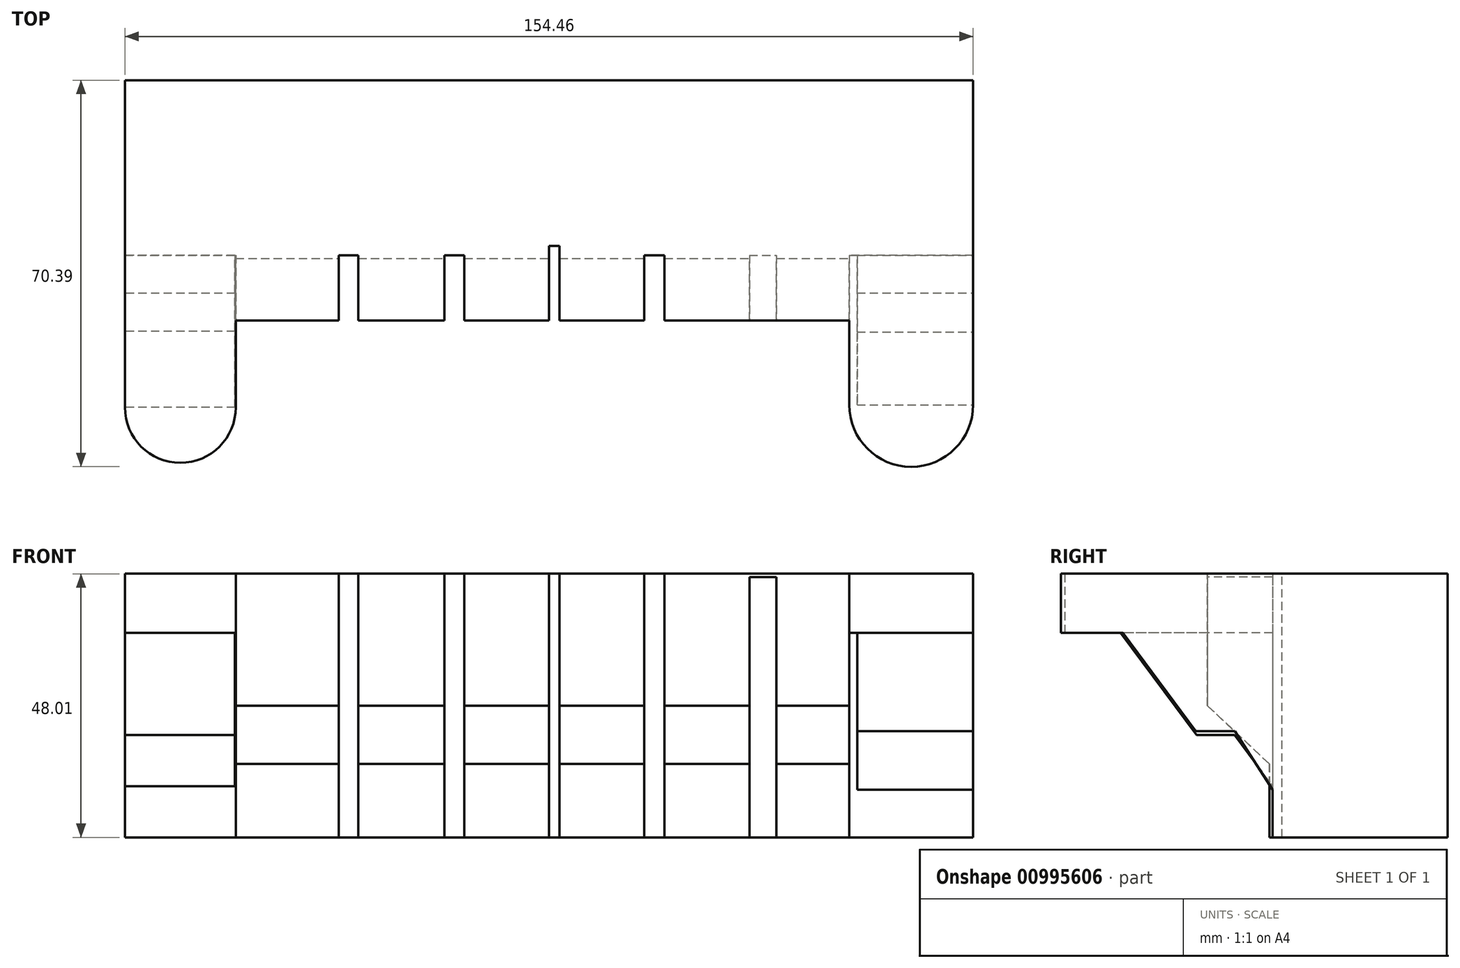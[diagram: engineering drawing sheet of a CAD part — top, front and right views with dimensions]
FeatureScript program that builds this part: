
annotation { "Feature Type Name" : "Feature", "Feature Type Description" : "" }
export const myFeature = defineFeature(function(context is Context, id is Id, definition is map)
    precondition{}
    {
        {
            var Q0;
            Q0=qCreatedBy(makeId("Top.planeOp"),FACE);
            var sketch = newSketch(context, id + "F0", { "sketchPlane" : qUnion([Q0])});
            skLineSegment(sketch, "E0.bottom", {"start": v(-77.23, 15.64) * mm, "end": v(77.23, 15.64) * mm});
            skLineSegment(sketch, "E0.top", {"start": v(-77.23, -16.82) * mm, "end": v(77.23, -16.82) * mm});
            skLineSegment(sketch, "E0.left", {"start": v(-77.23, 15.64) * mm, "end": v(-77.23, -16.82) * mm});
            skLineSegment(sketch, "E0.right", {"start": v(77.23, 15.64) * mm, "end": v(77.23, -16.82) * mm});
            skSolve(sketch);
        }
        {
            var Q0;
            Q0=makeQuery(id+"F0.imprint","IMPRINT",FACE,{"disambiguationData":[TD([[makeQuery(id+"F0.imprint","IMPRINT",EDGE,{"derivedFrom":sQuery(id+"F0.wireOp",EDGE,"E0.bottom")}),-1.0]])]});
            extrude(context, id + "F1", {"entities" : qUnion([Q0]), "depth" : 48 * mm, "offsetDistance" : 25.4 * mm});
        }
        {
            var Q0;
            Q0=makeQuery(id+"F1.opExtrude","SWEPT_FACE",FACE,{"disambiguationData":[OSD([sQuery(id+"F0.wireOp",EDGE,"E0.right")])]});
            var sketch = newSketch(context, id + "F2", { "sketchPlane" : qUnion([Q0])});
            skPoint(sketch, "E1.oppositeSnap0", {"position": v(15.64, 24) * mm});
            skLineSegment(sketch, "E1.bottom", {"start": v(-16.82, 48.01) * mm, "end": v(-28.1, 48.01) * mm});
            skLineSegment(sketch, "E1.top", {"start": v(-16.82, 24) * mm, "end": v(-28.1, 24) * mm});
            skLineSegment(sketch, "E1.left", {"start": v(-16.82, 48.01) * mm, "end": v(-16.82, 24) * mm});
            skLineSegment(sketch, "E1.right", {"start": v(-28.1, 48.01) * mm, "end": v(-28.1, 24) * mm});
            skLineSegment(sketch, "E2", {"start": v(-28.1, 24) * mm, "end": v(-16.45, 13.01) * mm});
            skLineSegment(sketch, "E3", {"start": v(-16.45, 13.01) * mm, "end": v(-16.82, 24) * mm});
            skSolve(sketch);
        }
        {
            var Q0;
            Q0=makeQuery(id+"F2.imprint","IMPRINT",FACE,{"disambiguationData":[TD([[makeQuery(id+"F2.imprint","IMPRINT",EDGE,{"derivedFrom":sQuery(id+"F2.wireOp",EDGE,"E1.bottom")}),1.0]])]});
            var Q1;
            {var subQ0=sQuery(id+"F2.wireOp",EDGE,"E1.top");Q1=makeQuery(id+"F2.imprint","IMPRINT",FACE,{"disambiguationData":[TD([[makeQuery(id+"F2.imprint","IMPRINT",EDGE,{"derivedFrom":subQ0}),1.0]])]});}
            extrude(context, id + "F3", {"entities" : qUnion([Q0, Q1]), "operationType" : NewBodyOperationType.ADD, "oppositeDirection" : true, "depth" : 154.68 * mm, "offsetDistance" : 25.4 * mm});
        }
        {
            var Q0;
            Q0=makeQuery(id+"F3.opExtrude","SWEPT_FACE",FACE,{"disambiguationData":[OSD([sQuery(id+"F2.wireOp",EDGE,"E1.right")])]});
            var sketch = newSketch(context, id + "F4", { "sketchPlane" : qUnion([Q0])});
            skLineSegment(sketch, "E4.bottom", {"start": v(-77.45, 48.01) * mm, "end": v(-57.04, 48.01) * mm});
            skLineSegment(sketch, "E4.top", {"start": v(-77.45, 0) * mm, "end": v(-57.04, 0) * mm});
            skLineSegment(sketch, "E4.left", {"start": v(-77.45, 48.01) * mm, "end": v(-77.45, 0) * mm});
            skLineSegment(sketch, "E4.right", {"start": v(-57.04, 48.01) * mm, "end": v(-57.04, 0) * mm});
            skLineSegment(sketch, "E5.bottom", {"start": v(77.23, 48.01) * mm, "end": v(54.67, 48.01) * mm});
            skLineSegment(sketch, "E5.top", {"start": v(77.23, 0) * mm, "end": v(54.67, 0) * mm});
            skLineSegment(sketch, "E5.left", {"start": v(77.23, 48.01) * mm, "end": v(77.23, 0) * mm});
            skLineSegment(sketch, "E5.right", {"start": v(54.67, 48.01) * mm, "end": v(54.67, 0) * mm});
            skLineSegment(sketch, "E6.bottom", {"start": v(-38.3, 48.01) * mm, "end": v(-34.74, 48.01) * mm});
            skLineSegment(sketch, "E6.top", {"start": v(-38.3, 0) * mm, "end": v(-34.74, 0) * mm});
            skLineSegment(sketch, "E6.left", {"start": v(-38.3, 48.01) * mm, "end": v(-38.3, 0) * mm});
            skLineSegment(sketch, "E6.right", {"start": v(-34.74, 48.01) * mm, "end": v(-34.74, 0) * mm});
            skLineSegment(sketch, "E7.bottom", {"start": v(-19.02, 48.01) * mm, "end": v(-15.44, 48.01) * mm});
            skLineSegment(sketch, "E7.top", {"start": v(-19.02, 0) * mm, "end": v(-15.44, 0) * mm});
            skLineSegment(sketch, "E7.left", {"start": v(-19.02, 48.01) * mm, "end": v(-19.02, 0) * mm});
            skLineSegment(sketch, "E7.right", {"start": v(-15.44, 48.01) * mm, "end": v(-15.44, 0) * mm});
            skLineSegment(sketch, "E8.bottom", {"start": v(-0.1, 48.01) * mm, "end": v(0, 48.01) * mm});
            skLineSegment(sketch, "E8.top", {"start": v(-0.1, 0) * mm, "end": v(0, 0) * mm});
            skLineSegment(sketch, "E8.left", {"start": v(-0.1, 48.01) * mm, "end": v(-0.1, 0) * mm});
            skLineSegment(sketch, "E8.right", {"start": v(0, 48.01) * mm, "end": v(0, 0) * mm});
            skLineSegment(sketch, "E9.bottom", {"start": v(17.33, 48.01) * mm, "end": v(21.02, 48.01) * mm});
            skLineSegment(sketch, "E9.top", {"start": v(17.33, 0) * mm, "end": v(21.02, 0) * mm});
            skLineSegment(sketch, "E9.left", {"start": v(17.33, 48.01) * mm, "end": v(17.33, 0) * mm});
            skLineSegment(sketch, "E9.right", {"start": v(21.02, 48.01) * mm, "end": v(21.02, 0) * mm});
            skLineSegment(sketch, "E10.bottom", {"start": v(36.5, 47.4) * mm, "end": v(41.4, 47.4) * mm});
            skLineSegment(sketch, "E10.top", {"start": v(36.5, 0) * mm, "end": v(41.4, 0) * mm});
            skLineSegment(sketch, "E10.left", {"start": v(36.5, 47.4) * mm, "end": v(36.5, 0) * mm});
            skLineSegment(sketch, "E10.right", {"start": v(41.4, 47.4) * mm, "end": v(41.4, 0) * mm});
            skSolve(sketch);
        }
        {
            var Q0;
            {var subQ0=sQuery(id+"F4.wireOp",EDGE,"E4.top");Q0=makeQuery(id+"F4.imprint","IMPRINT",FACE,{"disambiguationData":[TD([[makeQuery(id+"F4.imprint","IMPRINT",EDGE,{"derivedFrom":subQ0}),1.0]])]});}
            var Q1;
            {var subQ0=sQuery(id+"F4.wireOp",EDGE,"E4.bottom");Q1=makeQuery(id+"F4.imprint","IMPRINT",FACE,{"disambiguationData":[TD([[makeQuery(id+"F4.imprint","IMPRINT",EDGE,{"derivedFrom":subQ0}),-1.0]])]});}
            var Q2;
            {var subQ0=sQuery(id+"F4.wireOp",EDGE,"E6.top");Q2=makeQuery(id+"F4.imprint","IMPRINT",FACE,{"disambiguationData":[TD([[makeQuery(id+"F4.imprint","IMPRINT",EDGE,{"derivedFrom":subQ0}),1.0]])]});}
            var Q3;
            {var subQ0=sQuery(id+"F4.wireOp",EDGE,"E6.bottom");Q3=makeQuery(id+"F4.imprint","IMPRINT",FACE,{"disambiguationData":[TD([[makeQuery(id+"F4.imprint","IMPRINT",EDGE,{"derivedFrom":subQ0}),-1.0]])]});}
            var Q4;
            {var subQ0=sQuery(id+"F4.wireOp",EDGE,"E7.bottom");Q4=makeQuery(id+"F4.imprint","IMPRINT",FACE,{"disambiguationData":[TD([[makeQuery(id+"F4.imprint","IMPRINT",EDGE,{"derivedFrom":subQ0}),-1.0]])]});}
            var Q5;
            {var subQ0=sQuery(id+"F4.wireOp",EDGE,"E7.top");Q5=makeQuery(id+"F4.imprint","IMPRINT",FACE,{"disambiguationData":[TD([[makeQuery(id+"F4.imprint","IMPRINT",EDGE,{"derivedFrom":subQ0}),1.0]])]});}
            var Q6;
            {var subQ0=sQuery(id+"F4.wireOp",EDGE,"E9.bottom");Q6=makeQuery(id+"F4.imprint","IMPRINT",FACE,{"disambiguationData":[TD([[makeQuery(id+"F4.imprint","IMPRINT",EDGE,{"derivedFrom":subQ0}),-1.0]])]});}
            var Q7;
            {var subQ0=sQuery(id+"F4.wireOp",EDGE,"E9.top");Q7=makeQuery(id+"F4.imprint","IMPRINT",FACE,{"disambiguationData":[TD([[makeQuery(id+"F4.imprint","IMPRINT",EDGE,{"derivedFrom":subQ0}),1.0]])]});}
            var Q8;
            {var subQ0=sQuery(id+"F4.wireOp",EDGE,"E10.top");Q8=makeQuery(id+"F4.imprint","IMPRINT",FACE,{"disambiguationData":[TD([[makeQuery(id+"F4.imprint","IMPRINT",EDGE,{"derivedFrom":subQ0}),1.0]])]});}
            var Q9;
            {var subQ0=sQuery(id+"F4.wireOp",EDGE,"E5.bottom");Q9=makeQuery(id+"F4.imprint","IMPRINT",FACE,{"disambiguationData":[TD([[makeQuery(id+"F4.imprint","IMPRINT",EDGE,{"derivedFrom":subQ0}),-1.0]])]});}
            var Q10;
            {var subQ0=sQuery(id+"F4.wireOp",EDGE,"E5.top");Q10=makeQuery(id+"F4.imprint","IMPRINT",FACE,{"disambiguationData":[TD([[makeQuery(id+"F4.imprint","IMPRINT",EDGE,{"derivedFrom":subQ0}),-1.0]])]});}
            var Q11;
            {var subQ0=sQuery(id+"F4.wireOp",EDGE,"E10.bottom");Q11=makeQuery(id+"F4.imprint","IMPRINT",FACE,{"disambiguationData":[TD([[makeQuery(id+"F4.imprint","IMPRINT",EDGE,{"derivedFrom":subQ0}),-1.0]])]});}
            extrude(context, id + "F5", {"entities" : qUnion([Q0, Q1, Q2, Q3, Q4, Q5, Q6, Q7, Q8, Q9, Q10, Q11]), "operationType" : NewBodyOperationType.REMOVE, "oppositeDirection" : true, "depth" : 11.88 * mm, "offsetDistance" : 25.4 * mm});
        }
        {
            var Q0;
            Q0=makeQuery(id+"F3.boolean.opBoolean","MERGE",FACE,{"derivedFrom":[makeQuery(id+"F1.opExtrude","CAP_FACE",FACE,{"disambiguationData":[OSD([sQuery(id+"F0.wireOp",EDGE,"E0.bottom"),sQuery(id+"F0.wireOp",EDGE,"E0.top"),sQuery(id+"F0.wireOp",EDGE,"E0.left"),sQuery(id+"F0.wireOp",EDGE,"E0.right")])],"isStart":false}),makeQuery(id+"F3.opExtrude","SWEPT_FACE",FACE,{"disambiguationData":[OSD([sQuery(id+"F2.wireOp",EDGE,"E1.bottom")])]})]});
            var sketch = newSketch(context, id + "F6", { "sketchPlane" : qUnion([Q0])});
            skLineSegment(sketch, "E11.bottom", {"start": v(-77.23, -16.21) * mm, "end": v(-57.04, -16.21) * mm});
            skLineSegment(sketch, "E11.top", {"start": v(-77.23, -43.94) * mm, "end": v(-57.04, -43.94) * mm});
            skLineSegment(sketch, "E11.left", {"start": v(-77.23, -16.21) * mm, "end": v(-77.23, -43.94) * mm});
            skLineSegment(sketch, "E11.right", {"start": v(-57.04, -16.21) * mm, "end": v(-57.04, -43.94) * mm});
            skArc(sketch, "E12", {"start": v(-77.23, -43.94) * mm, "mid": v(-67.14, -54.03) * mm, "end": v(-57.04, -43.94) * mm});
            skPoint(sketch, "E13.oppositeSnap0", {"position": v(77.23, -0.29) * mm});
            skLineSegment(sketch, "E13.bottom", {"start": v(54.67, -16.21) * mm, "end": v(77.23, -16.21) * mm});
            skLineSegment(sketch, "E13.top", {"start": v(54.67, -43.47) * mm, "end": v(77.23, -43.47) * mm});
            skLineSegment(sketch, "E13.left", {"start": v(54.67, -16.21) * mm, "end": v(54.67, -43.47) * mm});
            skLineSegment(sketch, "E13.right", {"start": v(77.23, -16.21) * mm, "end": v(77.23, -43.47) * mm});
            skArc(sketch, "E14", {"start": v(54.67, -43.47) * mm, "mid": v(65.95, -54.75) * mm, "end": v(77.23, -43.47) * mm});
            skSolve(sketch);
        }
        {
            var Q0;
            {var subQ5=sQuery(id+"F6.wireOp",EDGE,"E11.bottom");Q0=makeQuery(id+"F6.imprint","IMPRINT",FACE,{"disambiguationData":[TD([[makeQuery(id+"F6.imprint","IMPRINT",EDGE,{"derivedFrom":subQ5}),-1.0]])]});}
            var Q1;
            Q1=makeQuery(id+"F6.imprint","IMPRINT",FACE,{"disambiguationData":[TD([[makeQuery(id+"F6.imprint","IMPRINT",EDGE,{"derivedFrom":sQuery(id+"F6.wireOp",EDGE,"E11.top")}),-1.0]])]});
            var Q2;
            Q2=makeQuery(id+"F6.imprint","IMPRINT",FACE,{"disambiguationData":[TD([[makeQuery(id+"F6.imprint","IMPRINT",EDGE,{"derivedFrom":sQuery(id+"F6.wireOp",EDGE,"E13.top")}),-1.0]])]});
            var Q3;
            {var subQ4=sQuery(id+"F6.wireOp",EDGE,"E13.bottom");Q3=makeQuery(id+"F6.imprint","IMPRINT",FACE,{"disambiguationData":[TD([[makeQuery(id+"F6.imprint","IMPRINT",EDGE,{"derivedFrom":subQ4}),-1.0]])]});}
            extrude(context, id + "F7", {"entities" : qUnion([Q0, Q1, Q2, Q3]), "operationType" : NewBodyOperationType.ADD, "oppositeDirection" : true, "depth" : 10.77 * mm, "offsetDistance" : 25.4 * mm});
        }
        {
            var Q0;
            Q0=makeQuery(id+"F7.boolean.opBoolean","MERGE",FACE,{"derivedFrom":[makeQuery(id+"F1.opExtrude","SWEPT_FACE",FACE,{"disambiguationData":[OSD([sQuery(id+"F0.wireOp",EDGE,"E0.left")])]}),makeQuery(id+"F7.opExtrude","SWEPT_FACE",FACE,{"disambiguationData":[OSD([sQuery(id+"F6.wireOp",EDGE,"E11.left")])]})]});
            var sketch = newSketch(context, id + "F8", { "sketchPlane" : qUnion([Q0])});
            skLineSegment(sketch, "E15", {"start": v(43.94, 37.24) * mm, "end": v(30.08, 18.62) * mm});
            skPoint(sketch, "E15.endSnap0", {"position": v(16.21, 18.62) * mm});
            skPoint(sketch, "E15.endSnap1", {"position": v(30.08, 37.24) * mm});
            skLineSegment(sketch, "E16", {"start": v(30.08, 18.62) * mm, "end": v(16.21, 18.62) * mm});
            skLineSegment(sketch, "E17", {"start": v(23.14, 18.62) * mm, "end": v(16.21, 9.31) * mm});
            skLineSegment(sketch, "E18", {"start": v(16.21, 9.31) * mm, "end": v(16.21, 37.24) * mm});
            skLineSegment(sketch, "E19", {"start": v(16.21, 37.24) * mm, "end": v(43.94, 37.24) * mm});
            skSolve(sketch);
        }
        {
            var Q0;
            {var subQ5=sQuery(id+"F8.wireOp",EDGE,"E15");Q0=makeQuery(id+"F8.imprint","IMPRINT",FACE,{"disambiguationData":[TD([[makeQuery(id+"F8.imprint","IMPRINT",EDGE,{"derivedFrom":subQ5}),-1.0]])]});}
            var Q1;
            {var subQ3=sQuery(id+"F8.wireOp",EDGE,"E17");Q1=makeQuery(id+"F8.imprint","IMPRINT",FACE,{"disambiguationData":[TD([[makeQuery(id+"F8.imprint","IMPRINT",EDGE,{"derivedFrom":subQ3}),-1.0]])]});}
            extrude(context, id + "F9", {"entities" : qUnion([Q0, Q1]), "operationType" : NewBodyOperationType.ADD, "oppositeDirection" : true, "depth" : 20.05 * mm, "offsetDistance" : 25.4 * mm});
        }
        {
            var Q0;
            {var subQ0=sQuery(id+"F0.wireOp",EDGE,"E0.right");Q0=makeQuery(id+"F7.boolean.opBoolean","MERGE",FACE,{"derivedFrom":[makeQuery(id+"F3.boolean.opBoolean","MERGE",FACE,{"derivedFrom":[makeQuery(id+"F1.opExtrude","SWEPT_FACE",FACE,{"disambiguationData":[OSD([subQ0])]}),makeQuery(id+"F3.opExtrude","CAP_FACE",FACE,{"disambiguationData":[OSD([sQuery(id+"F0.wireOp",EDGE,"E0.top"),subQ0,sQuery(id+"F2.wireOp",EDGE,"E1.bottom"),sQuery(id+"F2.wireOp",EDGE,"E1.left"),sQuery(id+"F2.wireOp",EDGE,"E1.right"),sQuery(id+"F2.wireOp",EDGE,"E2")])],"isStart":true})]}),makeQuery(id+"F7.opExtrude","SWEPT_FACE",FACE,{"disambiguationData":[OSD([sQuery(id+"F6.wireOp",EDGE,"E13.right")])]})]});}
            var sketch = newSketch(context, id + "F10", { "sketchPlane" : qUnion([Q0])});
            skLineSegment(sketch, "E20", {"start": v(-43.47, 37.24) * mm, "end": v(-16.21, 37.24) * mm});
            skLineSegment(sketch, "E21", {"start": v(-16.21, 37.24) * mm, "end": v(-16.19, 8.63) * mm});
            skLineSegment(sketch, "E22", {"start": v(-43.47, 37.24) * mm, "end": v(-30.22, 19.32) * mm});
            skLineSegment(sketch, "E23", {"start": v(-30.22, 19.32) * mm, "end": v(-23.1, 19.32) * mm});
            skLineSegment(sketch, "E24", {"start": v(-23.1, 19.32) * mm, "end": v(-16.19, 8.63) * mm});
            skSolve(sketch);
        }
        {
            var Q0;
            {var subQ4=sQuery(id+"F10.wireOp",EDGE,"E20");Q0=makeQuery(id+"F10.imprint","IMPRINT",FACE,{"disambiguationData":[TD([[makeQuery(id+"F10.imprint","IMPRINT",EDGE,{"derivedFrom":subQ4}),1.0]])]});}
            extrude(context, id + "F11", {"entities" : qUnion([Q0]), "operationType" : NewBodyOperationType.ADD, "oppositeDirection" : true, "depth" : 21.13 * mm, "offsetDistance" : 25.4 * mm});
        }
        {
            var Q0;
            Q0=makeQuery(id+"F5.boolean.opBoolean","SPLIT",FACE,{"disambiguationData":[TD([makeQuery(id+"F5.opExtrude","SWEPT_FACE",FACE,{"disambiguationData":[OSD([sQuery(id+"F4.wireOp",EDGE,"E7.right")])]})])],"derivedFrom":makeQuery(id+"F3.opExtrude","SWEPT_FACE",FACE,{"disambiguationData":[OSD([sQuery(id+"F2.wireOp",EDGE,"E1.right")])]})});
            var sketch = newSketch(context, id + "F12", { "sketchPlane" : qUnion([Q0])});
            skLineSegment(sketch, "E25.bottom", {"start": v(0, 0) * mm, "end": v(1.9, 0) * mm});
            skLineSegment(sketch, "E25.top", {"start": v(0, 48.01) * mm, "end": v(1.9, 48.01) * mm});
            skLineSegment(sketch, "E25.left", {"start": v(0, 0) * mm, "end": v(0, 48.01) * mm});
            skLineSegment(sketch, "E25.right", {"start": v(1.9, 0) * mm, "end": v(1.9, 48.01) * mm});
            skPoint(sketch, "E25.middle", {"position": v(0.95, 24) * mm});
            skSolve(sketch);
        }
        {
            var Q0;
            {var subQ0=sQuery(id+"F12.wireOp",EDGE,"E25.top");Q0=makeQuery(id+"F12.imprint","IMPRINT",FACE,{"disambiguationData":[TD([[makeQuery(id+"F12.imprint","IMPRINT",EDGE,{"derivedFrom":subQ0}),-1.0]])]});}
            var Q1;
            {var subQ0=sQuery(id+"F12.wireOp",EDGE,"E25.bottom");Q1=makeQuery(id+"F12.imprint","IMPRINT",FACE,{"disambiguationData":[TD([[makeQuery(id+"F12.imprint","IMPRINT",EDGE,{"derivedFrom":subQ0}),1.0]])]});}
            extrude(context, id + "F13", {"entities" : qUnion([Q0, Q1]), "operationType" : NewBodyOperationType.REMOVE, "oppositeDirection" : true, "depth" : 13.6 * mm, "offsetDistance" : 25.4 * mm});
        }
    });
